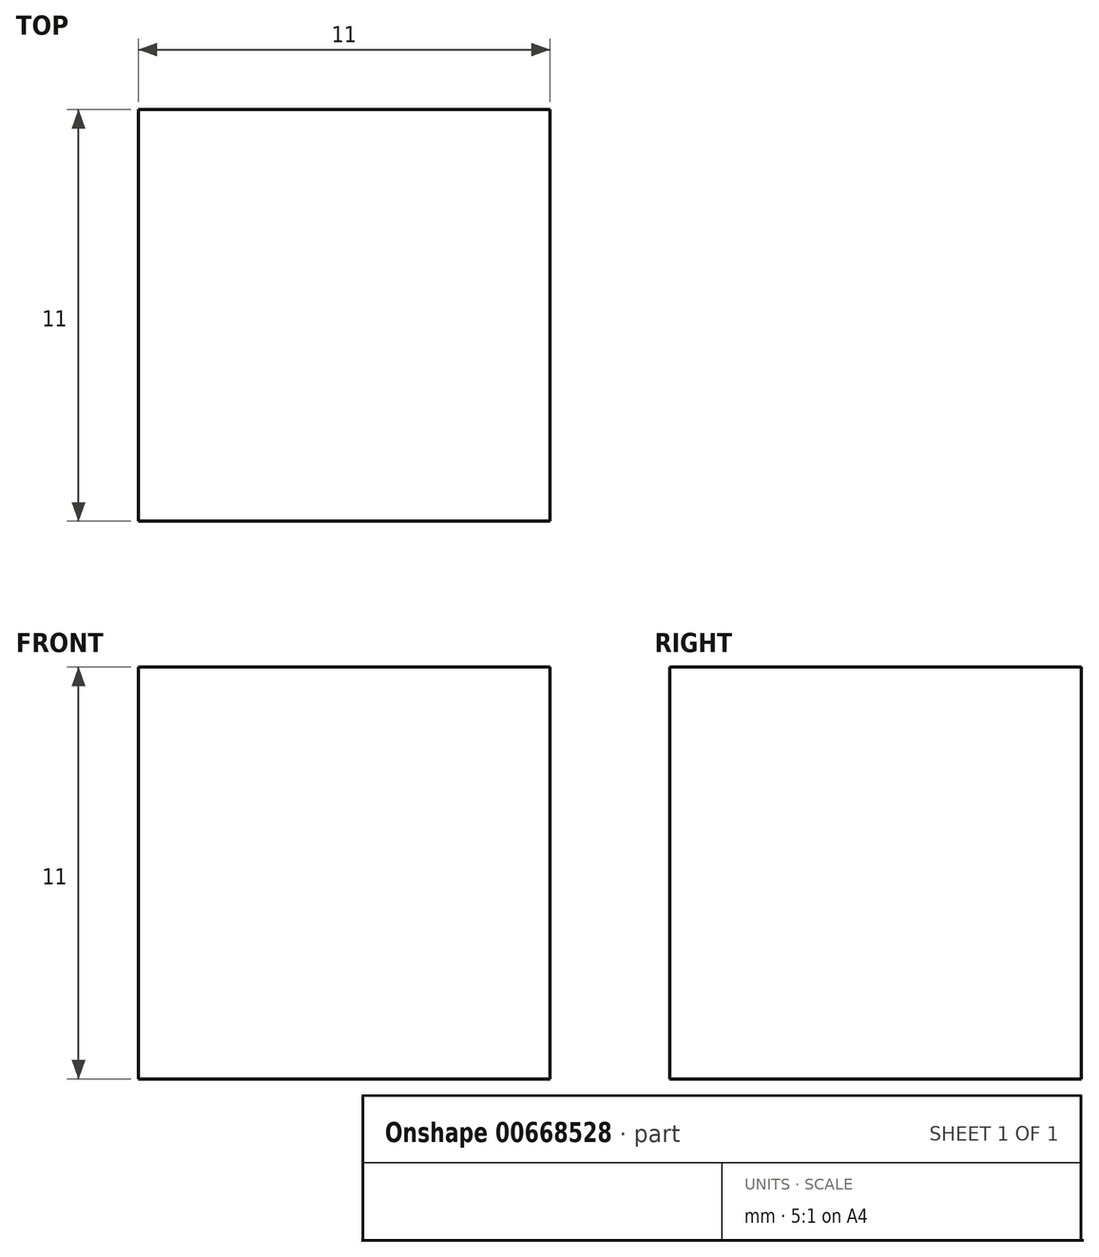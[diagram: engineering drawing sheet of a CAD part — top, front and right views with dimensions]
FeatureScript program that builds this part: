
annotation { "Feature Type Name" : "Feature", "Feature Type Description" : "" }
export const myFeature = defineFeature(function(context is Context, id is Id, definition is map)
    precondition{}
    {
        {
            var Q0;
            Q0=qCreatedBy(makeId("Front.planeOp"),FACE);
            var sketch = newSketch(context, id + "F0", { "sketchPlane" : qUnion([Q0])});
            skLineSegment(sketch, "E0.bottom", {"start": v(0, 0) * mm, "end": v(11, 0) * mm});
            skLineSegment(sketch, "E0.top", {"start": v(0, 11) * mm, "end": v(11, 11) * mm});
            skLineSegment(sketch, "E0.left", {"start": v(0, 0) * mm, "end": v(0, 11) * mm});
            skLineSegment(sketch, "E0.right", {"start": v(11, 0) * mm, "end": v(11, 11) * mm});
            skSolve(sketch);
        }
        {
            var Q0;
            Q0=makeQuery(id+"F0.imprint","IMPRINT",FACE,{"disambiguationData":[TD([[makeQuery(id+"F0.imprint","IMPRINT",EDGE,{"derivedFrom":sQuery(id+"F0.wireOp",EDGE,"E0.bottom")}),1.0]])]});
            extrude(context, id + "F1", {"entities" : qUnion([Q0]), "depth" : 11 * mm, "offsetDistance" : 25 * mm});
        }
    });
